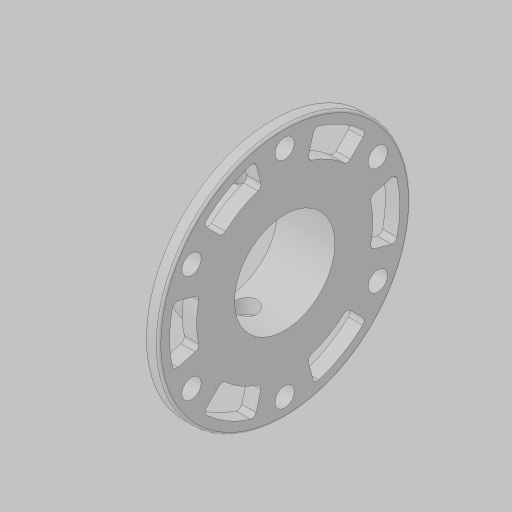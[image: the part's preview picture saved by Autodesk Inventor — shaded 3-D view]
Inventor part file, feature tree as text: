
AUTODESK INVENTOR PART (.ipt)
format: ipt  version: 2023.5 (Build 275446000, 446)  size: 232,960 bytes
history: native  units: in
note: dims shown in document units (in); Inventor stores cm internally (conversion verified against a paired STEP export)
features: sketch x2, hole x2, extrude x1, other x1
ambient origin geometry x8: Origin, YZ Plane, XZ Plane, XY Plane, X Axis, Y Axis, Z Axis, Center Point
bodies: Solid1 (feature_tree)
feature tree (6):
  extrude  "Extrusion1"  Depth=1.0in TaperAngle=0.0deg
  sketch  "Sketch2"  dims[d3=0.1562in d4=0.201in d5=0.38in d6=0.385in d7=0.25in d8=0.563in d9=1.0in d10=0.8108in d11=0.201in d12=0.75in d13=0.375in d14=0.25in d15=0.5635in d16=1.0in d17=0.8108in]
  hole  "Hole1"  [1 undecoded]
  hole  "Hole2"  [1 undecoded]
  sketch  "Sketch1"  dims[d0=0.875in d1=1.0in d2=0.0in]
  other  "Cut-Extrude8"
note: 2 required parameter values undecoded (feature->parameter linkage not recoverable at this tier; creation-order binding heuristic only, values carry confidence <= 0.55)
